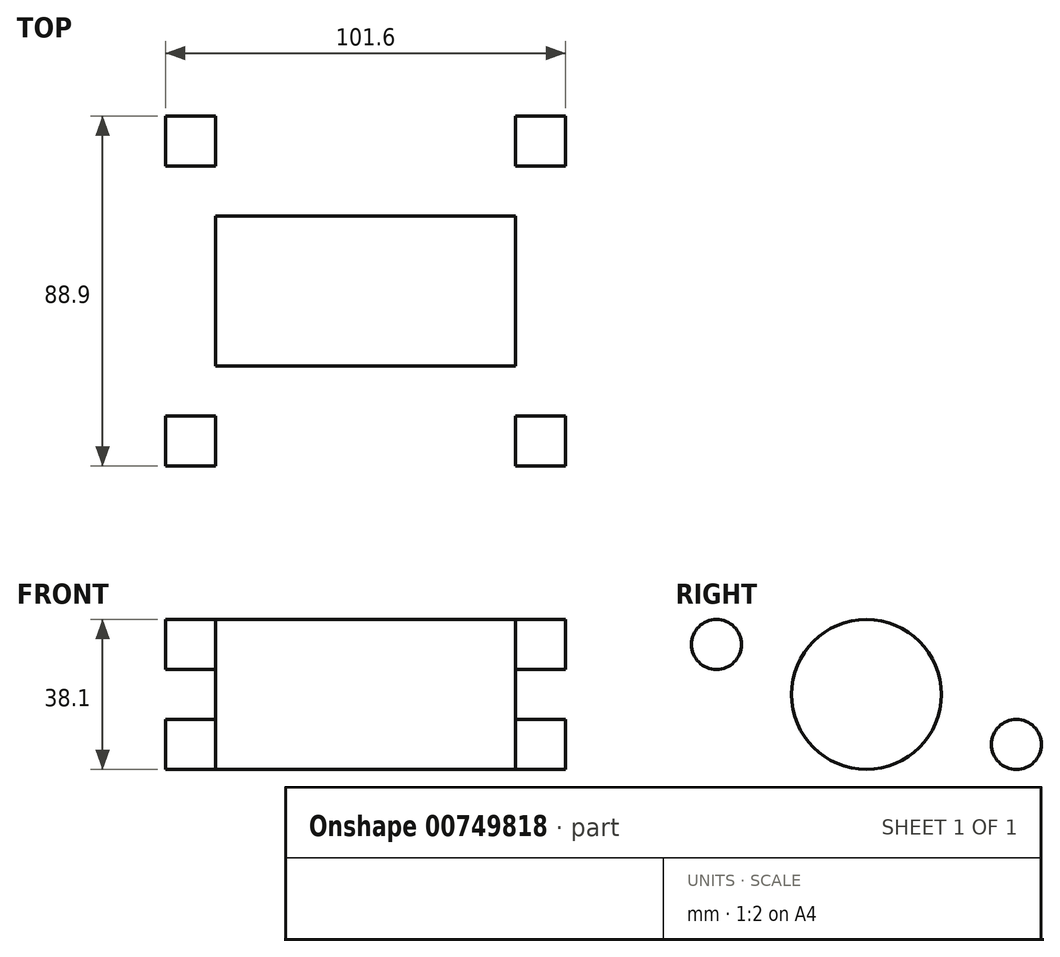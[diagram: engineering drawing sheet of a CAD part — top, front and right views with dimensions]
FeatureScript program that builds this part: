
annotation { "Feature Type Name" : "Feature", "Feature Type Description" : "" }
export const myFeature = defineFeature(function(context is Context, id is Id, definition is map)
    precondition{}
    {
        {
            var Q0;
            Q0=qCreatedBy(makeId("Right.planeOp"),FACE);
            var sketch = newSketch(context, id + "F0", { "sketchPlane" : qUnion([Q0])});
            skCircle(sketch, "E0", {"center": v(0, 0) * mm, "radius": 23.3 * mm});
            skSolve(sketch);
        }
        {
            var Q0;
            Q0=makeQuery(id+"F0.imprint","IMPRINT",FACE,{"disambiguationData":[TD([[makeQuery(id+"F0.imprint","IMPRINT",EDGE,{"derivedFrom":sQuery(id+"F0.wireOp",EDGE,"E0")}),1.0]])]});
            extrude(context, id + "F1", {"entities" : qUnion([Q0]), "depth" : 76.2 * mm, "offsetDistance" : 25.4 * mm});
        }
        {
            var Q0;
            Q0=makeQuery(id+"F1.opExtrude","CAP_FACE",FACE,{"disambiguationData":[OSD([sQuery(id+"F0.wireOp",EDGE,"E0")])],"isStart":false});
            var sketch = newSketch(context, id + "F2", { "sketchPlane" : qUnion([Q0])});
            skSolve(sketch);
        }
        {
            var Q0;
            Q0=makeQuery(id+"F2.imprint","IMPRINT",FACE,{"disambiguationData":[TD([[makeQuery(id+"F2.imprint","IMPRINT",EDGE,{"derivedFrom":makeQuery(id+"F1.opExtrude","CAP_EDGE",EDGE,{"disambiguationData":[OSD([sQuery(id+"F0.wireOp",EDGE,"E0")])],"isStart":false})}),1.0]])]});
            var sketch = newSketch(context, id + "F3", { "sketchPlane" : qUnion([Q0])});
            skCircle(sketch, "E1", {"center": v(0, 0) * mm, "radius": 50.8 * mm});
            skSolve(sketch);
        }
        {
            var Q0;
            Q0=makeQuery(id+"F3.imprint","IMPRINT",FACE,{"disambiguationData":[TD([[makeQuery(id+"F3.imprint","IMPRINT",EDGE,{"derivedFrom":sQuery(id+"F3.wireOp",EDGE,"E1")}),1.0]])]});
            extrude(context, id + "F4", {"entities" : qUnion([Q0]), "depth" : 12.7 * mm, "offsetDistance" : 25.4 * mm});
        }
        {
            var Q0;
            Q0=qCreatedBy(makeId("Front.planeOp"),FACE);
            var sketch = newSketch(context, id + "F5", { "sketchPlane" : qUnion([Q0])});
            skLineSegment(sketch, "E2", {"start": v(0, 0) * mm, "end": v(38.1, 0) * mm});
            skLineSegment(sketch, "E3", {"start": v(38.1, 0) * mm, "end": v(38.1, 39.2) * mm});
            skLineSegment(sketch, "E4", {"start": v(38.1, 39.2) * mm, "end": v(38.1, -66.9) * mm});
            skSolve(sketch);
        }
        {
            var Q0;
            Q0=makeQuery(id+"F1.opExtrude","CAP_FACE",FACE,{"disambiguationData":[OSD([sQuery(id+"F0.wireOp",EDGE,"E0")])],"isStart":true});
            var sketch = newSketch(context, id + "F6", { "sketchPlane" : qUnion([Q0])});
            skCircle(sketch, "E5", {"center": v(0, 0) * mm, "radius": 50.8 * mm});
            skSolve(sketch);
        }
        {
            var Q0;
            Q0=makeQuery(id+"F6.imprint","IMPRINT",FACE,{"disambiguationData":[TD([[makeQuery(id+"F6.imprint","IMPRINT",EDGE,{"derivedFrom":sQuery(id+"F6.wireOp",EDGE,"E5")}),1.0]])]});
            extrude(context, id + "F7", {"entities" : qUnion([Q0]), "depth" : 12.7 * mm, "offsetDistance" : 25.4 * mm});
        }
        {
            var Q0;
            Q0=makeQuery(id+"F2.imprint","IMPRINT",FACE,{"disambiguationData":[TD([[makeQuery(id+"F2.imprint","IMPRINT",EDGE,{"derivedFrom":makeQuery(id+"F1.opExtrude","CAP_EDGE",EDGE,{"disambiguationData":[OSD([sQuery(id+"F0.wireOp",EDGE,"E0")])],"isStart":false})}),1.0]])]});
            var sketch = newSketch(context, id + "F8", { "sketchPlane" : qUnion([Q0])});
            skCircle(sketch, "E6", {"center": v(0, 0) * mm, "radius": 19.05 * mm});
            skSolve(sketch);
        }
        {
            var Q0;
            Q0=makeQuery(id+"F8.imprint","IMPRINT",FACE,{"disambiguationData":[TD([[makeQuery(id+"F8.imprint","IMPRINT",EDGE,{"derivedFrom":sQuery(id+"F8.wireOp",EDGE,"E6")}),-1.0]])]});
            extrude(context, id + "F9", {"entities" : qUnion([Q0]), "operationType" : NewBodyOperationType.ADD, "depth" : 12.7 * mm, "offsetDistance" : 25.4 * mm});
        }
        {
            var Q0;
            Q0=makeQuery(id+"F1.opExtrude","CAP_FACE",FACE,{"disambiguationData":[OSD([sQuery(id+"F0.wireOp",EDGE,"E0")])],"isStart":true});
            var sketch = newSketch(context, id + "F10", { "sketchPlane" : qUnion([Q0])});
            skCircle(sketch, "E7", {"center": v(0, 0) * mm, "radius": 19.05 * mm});
            skSolve(sketch);
        }
        {
            var Q0;
            Q0=makeQuery(id+"F10.imprint","IMPRINT",FACE,{"disambiguationData":[TD([[makeQuery(id+"F10.imprint","IMPRINT",EDGE,{"derivedFrom":sQuery(id+"F10.wireOp",EDGE,"E7")}),-1.0]])]});
            extrude(context, id + "F11", {"entities" : qUnion([Q0]), "operationType" : NewBodyOperationType.ADD, "depth" : 12.7 * mm, "offsetDistance" : 25.4 * mm});
        }
        {
            var Q0;
            {var subQ0=sQuery(id+"F0.wireOp",EDGE,"E0");Q0=makeQuery(id+"F11.boolean.opBoolean","MERGE",FACE,{"derivedFrom":[makeQuery(id+"F7.opExtrude","CAP_FACE",FACE,{"disambiguationData":[OSD([subQ0,sQuery(id+"F6.wireOp",EDGE,"E5")])],"isStart":false}),makeQuery(id+"F11.opExtrude","CAP_FACE",FACE,{"disambiguationData":[OSD([subQ0,sQuery(id+"F10.wireOp",EDGE,"E7")])],"isStart":false})]});}
            var sketch = newSketch(context, id + "F12", { "sketchPlane" : qUnion([Q0])});
            skLineSegment(sketch, "E8", {"start": v(0, 50.8) * mm, "end": v(-38.1, 50.8) * mm, "construction": true});
            skLineSegment(sketch, "E9", {"start": v(-38.1, 50.8) * mm, "end": v(-38.1, 12.7) * mm, "construction": true});
            skCircle(sketch, "E10", {"center": v(-38.1, 12.7) * mm, "radius": 6.35 * mm});
            skCircle(sketch, "E11.MirrorC", {"center": v(-38.1, -12.7) * mm, "radius": 6.35 * mm});
            skCircle(sketch, "E12.MirrorC", {"center": v(38.1, -12.7) * mm, "radius": 6.35 * mm});
            skCircle(sketch, "E13.MirrorC", {"center": v(38.1, 12.7) * mm, "radius": 6.35 * mm});
            skSolve(sketch);
        }
        {
            var Q0;
            Q0=makeQuery(id+"F12.imprint","IMPRINT",FACE,{"disambiguationData":[TD([[makeQuery(id+"F12.imprint","IMPRINT",EDGE,{"derivedFrom":sQuery(id+"F12.wireOp",EDGE,"E10")}),1.0]])]});
            var Q1;
            Q1=makeQuery(id+"F12.imprint","IMPRINT",FACE,{"disambiguationData":[TD([[makeQuery(id+"F12.imprint","IMPRINT",EDGE,{"derivedFrom":sQuery(id+"F12.wireOp",EDGE,"E11.MirrorC")}),-1.0]])]});
            var Q2;
            Q2=makeQuery(id+"F12.imprint","IMPRINT",FACE,{"disambiguationData":[TD([[makeQuery(id+"F12.imprint","IMPRINT",EDGE,{"derivedFrom":sQuery(id+"F12.wireOp",EDGE,"E12.MirrorC")}),1.0]])]});
            var Q3;
            Q3=makeQuery(id+"F12.imprint","IMPRINT",FACE,{"disambiguationData":[TD([[makeQuery(id+"F12.imprint","IMPRINT",EDGE,{"derivedFrom":sQuery(id+"F12.wireOp",EDGE,"E13.MirrorC")}),-1.0]])]});
            extrude(context, id + "F13", {"entities" : qUnion([Q0, Q1, Q2, Q3]), "operationType" : NewBodyOperationType.REMOVE, "oppositeDirection" : true, "depth" : 2540 * mm, "offsetDistance" : 25.4 * mm});
        }
    });
